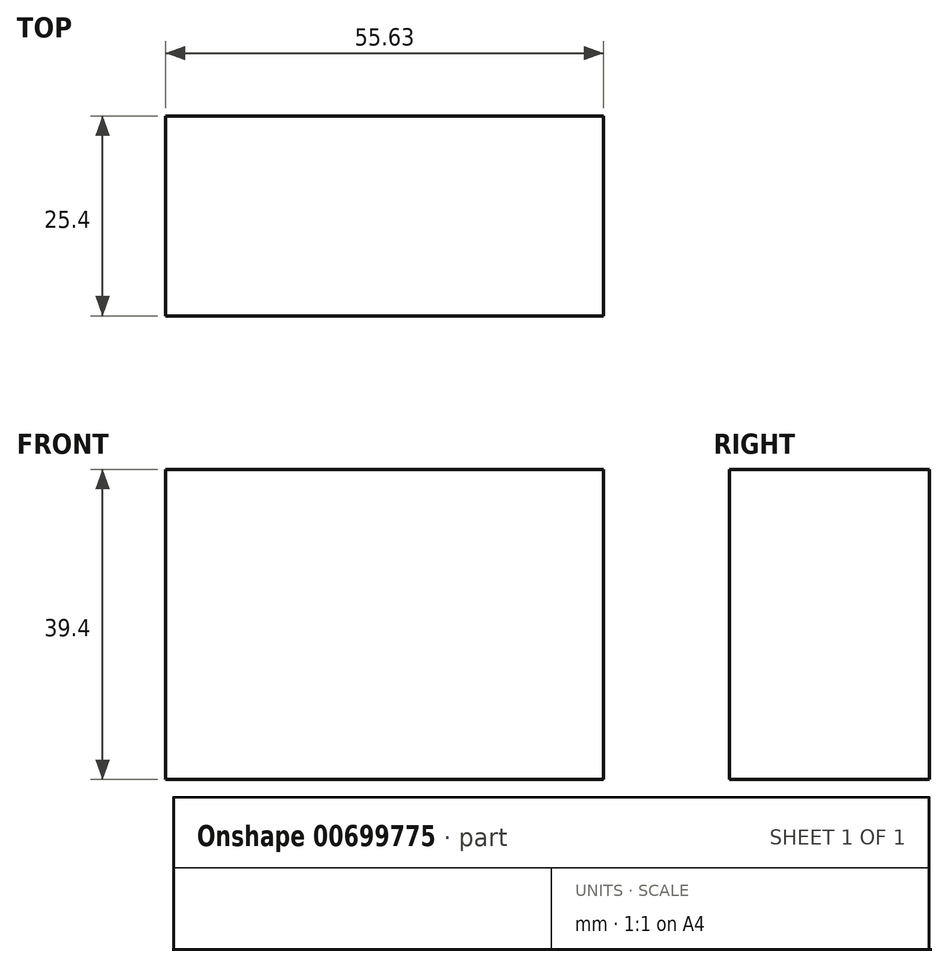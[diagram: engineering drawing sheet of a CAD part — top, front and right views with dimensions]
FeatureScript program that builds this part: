
annotation { "Feature Type Name" : "Feature", "Feature Type Description" : "" }
export const myFeature = defineFeature(function(context is Context, id is Id, definition is map)
    precondition{}
    {
        {
            var Q0;
            Q0=qCreatedBy(makeId("Front.planeOp"),FACE);
            var sketch = newSketch(context, id + "F0", { "sketchPlane" : qUnion([Q0])});
            skLineSegment(sketch, "E0", {"start": v(-57.34, 39.4) * mm, "end": v(-57.34, 0) * mm});
            skLineSegment(sketch, "E1", {"start": v(-57.34, 0) * mm, "end": v(-1.71, 0) * mm});
            skLineSegment(sketch, "E2", {"start": v(-1.71, 0) * mm, "end": v(-1.71, 39.4) * mm});
            skLineSegment(sketch, "E3", {"start": v(-1.71, 39.4) * mm, "end": v(-57.34, 39.4) * mm});
            skSolve(sketch);
        }
        {
            var Q0;
            Q0=makeQuery(id+"F0.imprint","IMPRINT",FACE,{"disambiguationData":[TD([[makeQuery(id+"F0.imprint","IMPRINT",EDGE,{"derivedFrom":sQuery(id+"F0.wireOp",EDGE,"E0")}),1.0]])]});
            extrude(context, id + "F1", {"entities" : qUnion([Q0]), "depth" : 25.4 * mm, "offsetDistance" : 25.4 * mm});
        }
    });
